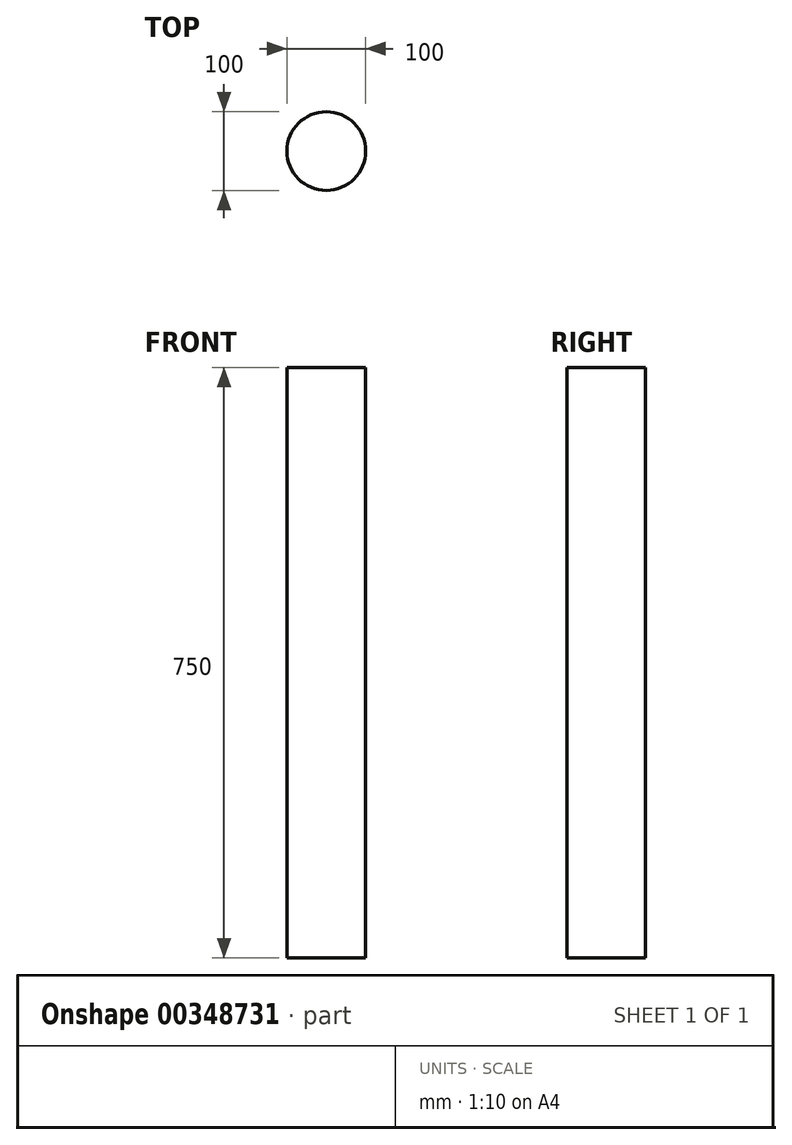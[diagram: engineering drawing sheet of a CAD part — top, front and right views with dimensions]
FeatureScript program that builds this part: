
annotation { "Feature Type Name" : "Feature", "Feature Type Description" : "" }
export const myFeature = defineFeature(function(context is Context, id is Id, definition is map)
    precondition{}
    {
        {
            var Q0;
            Q0=qCreatedBy(makeId("Top.planeOp"),FACE);
            var sketch = newSketch(context, id + "F0", { "sketchPlane" : qUnion([Q0])});
            skCircle(sketch, "E0", {"center": v(0, 0) * mm, "radius": 50 * mm});
            skSolve(sketch);
        }
        {
            var Q0;
            Q0=makeQuery(id+"F0.imprint","IMPRINT",FACE,{"disambiguationData":[TD([[makeQuery(id+"F0.imprint","IMPRINT",EDGE,{"derivedFrom":sQuery(id+"F0.wireOp",EDGE,"E0")}),1.0]])]});
            extrude(context, id + "F1", {"entities" : qUnion([Q0]), "depth" : 750 * mm});
        }
    });
